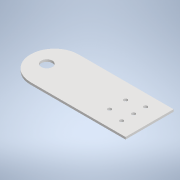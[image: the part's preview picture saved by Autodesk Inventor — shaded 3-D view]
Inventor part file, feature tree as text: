
AUTODESK INVENTOR PART (.ipt)
format: ipt  version: 2022 (Build 260153000, 153)  size: 135,168 bytes
history: native  units: mm
features: sheet_metal_op x1, sketch x1, other x1
ambient origin geometry x8: Origin, YZ Plane, XZ Plane, XY Plane, X Axis, Y Axis, Z Axis, Center Point
bodies: Body1 (feature_tree)
feature tree (3):
  sheet_metal_op  "Face3"
  sketch  "Sketch2"  dims[d36=44.0mm d37=44.0mm d38=65.0mm d41=10.2mm d42=22.0mm d43=15.0mm d44=14.666667mm d45=14.666667mm d46=14.666667mm d47=11.0mm d48=11.0mm d49=11.0mm d50=11.0mm d51=3.35mm d52=3.35mm d53=3.35mm d54=3.35mm d55=3.35mm d56=14.666667mm d57=14.666667mm d58=14.666667mm d59=14.666667mm d60=2.0mm]
  other  "Plate3"
